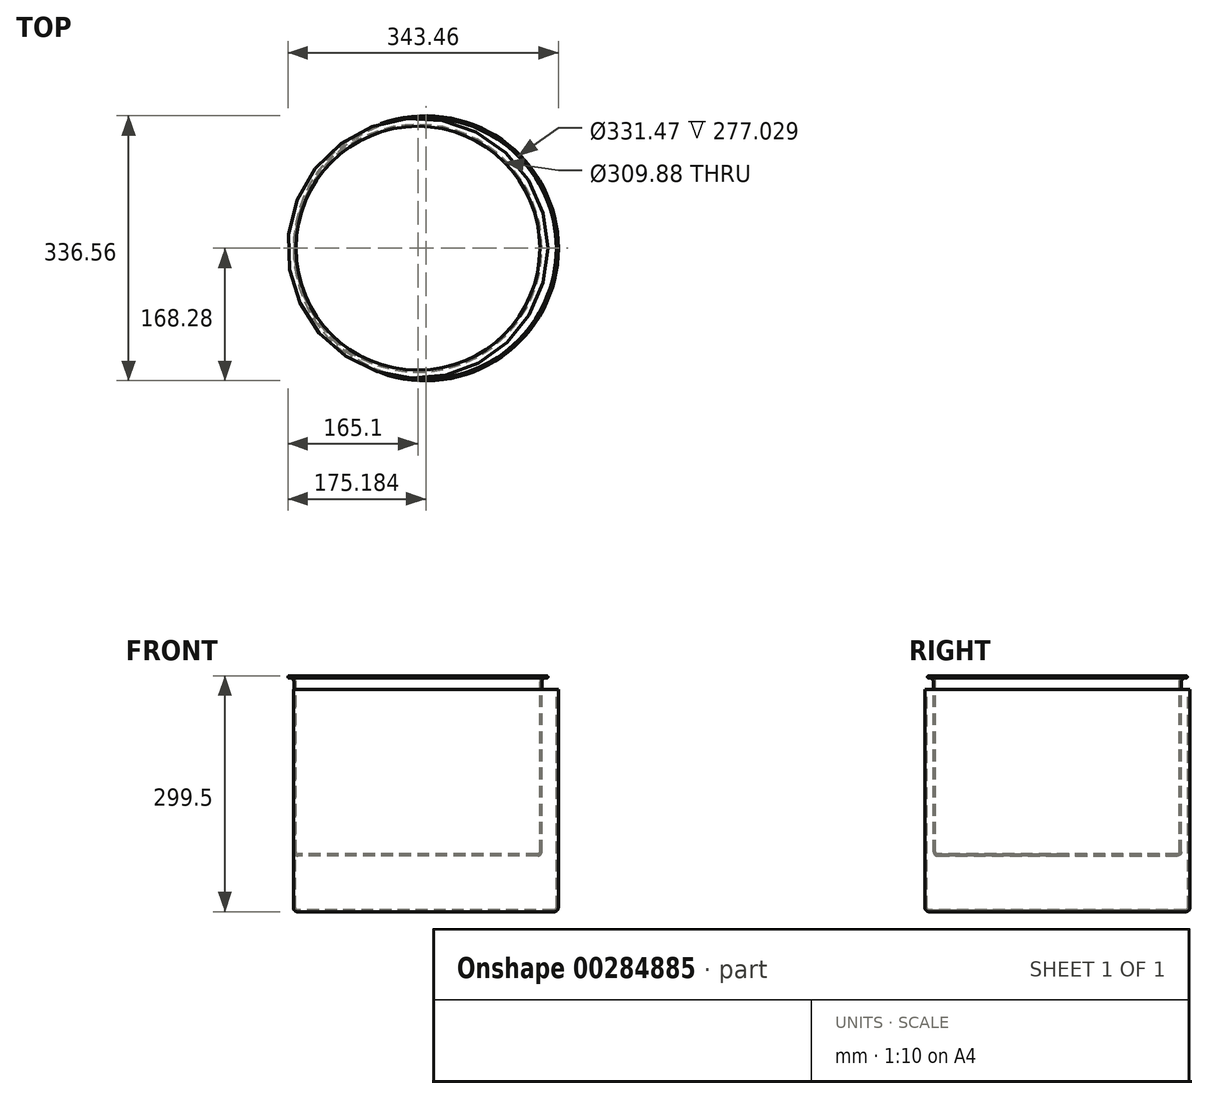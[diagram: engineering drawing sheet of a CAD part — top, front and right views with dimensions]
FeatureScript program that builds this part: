
annotation { "Feature Type Name" : "Feature", "Feature Type Description" : "" }
export const myFeature = defineFeature(function(context is Context, id is Id, definition is map)
    precondition{}
    {
        {
            var Q0;
            Q0=qCreatedBy(makeId("Top.planeOp"),FACE);
            var sketch = newSketch(context, id + "F0", { "sketchPlane" : qUnion([Q0])});
            skCircle(sketch, "E0", {"center": v(0, 0) * mm, "radius": 165.1 * mm});
            skSolve(sketch);
        }
        {
            var Q0;
            Q0 = qSketchRegion(id + "F0", true);
            extrude(context, id + "F1", {"entities" : qUnion([Q0]), "depth" : 2.54 * mm});
        }
        {
            var Q0;
            Q0=makeQuery(id+"F1.opExtrude","CAP_FACE",FACE,{"disambiguationData":[OSD([sQuery(id+"F0.wireOp",EDGE,"E0")])],"isStart":false});
            var sketch = newSketch(context, id + "F2", { "sketchPlane" : qUnion([Q0])});
            skCircle(sketch, "E1", {"center": v(0, 0) * mm, "radius": 165.1 * mm});
            skCircle(sketch, "E2.0", {"center": v(0, 0) * mm, "radius": 162.56 * mm});
            skSolve(sketch);
        }
        {
            var Q0;
            Q0 = qSketchRegion(id + "F2", true);
            extrude(context, id + "F3", {"entities" : qUnion([Q0]), "operationType" : NewBodyOperationType.ADD, "depth" : 228.6 * mm});
        }
        {
            var Q0;
            Q0=qCreatedBy(makeId("Front.planeOp"),FACE);
            var sketch = newSketch(context, id + "F4", { "sketchPlane" : qUnion([Q0])});
            skLineSegment(sketch, "E3", {"start": v(0, 0) * mm, "end": v(-152.4, 0) * mm});
            skLineSegment(sketch, "E4", {"start": v(-157.48, 5.08) * mm, "end": v(-157.48, 220.98) * mm});
            skLineSegment(sketch, "E5", {"start": v(-162.56, 226.06) * mm, "end": v(-163.83, 226.06) * mm});
            skPoint(sketch, "E6.visualSharp", {"position": v(-157.48, 226.06) * mm});
            skArc(sketch, "E6.filletArc", {"start": v(-157.48, 220.98) * mm, "mid": v(-158.97, 224.57) * mm, "end": v(-162.56, 226.06) * mm});
            skPoint(sketch, "E7.visualSharp", {"position": v(-157.48, 0) * mm});
            skArc(sketch, "E7.filletArc", {"start": v(-157.48, 5.08) * mm, "mid": v(-156, 1.49) * mm, "end": v(-152.4, 0) * mm});
            skLineSegment(sketch, "E8.0", {"start": v(-162.56, 228.6) * mm, "end": v(-163.83, 228.6) * mm});
            skArc(sketch, "E8.1", {"start": v(-154.94, 220.98) * mm, "mid": v(-157.17, 226.37) * mm, "end": v(-162.56, 228.6) * mm});
            skLineSegment(sketch, "E8.2", {"start": v(-154.94, 5.08) * mm, "end": v(-154.94, 220.98) * mm});
            skLineSegment(sketch, "E8.3", {"start": v(0, 2.54) * mm, "end": v(-152.4, 2.54) * mm});
            skPoint(sketch, "E9.visualSharp", {"position": v(-154.94, 2.54) * mm});
            skArc(sketch, "E9.filletArc", {"start": v(-154.94, 5.08) * mm, "mid": v(-154.2, 3.28) * mm, "end": v(-152.4, 2.54) * mm});
            skLineSegment(sketch, "E10", {"start": v(0, 2.54) * mm, "end": v(0, 0) * mm});
            skLineSegment(sketch, "E11", {"start": v(-165.1, 227.33) * mm, "end": v(-165.1, 227.33) * mm});
            skPoint(sketch, "E12.visualSharp", {"position": v(-165.1, 228.6) * mm});
            skArc(sketch, "E12.filletArc", {"start": v(-163.83, 228.6) * mm, "mid": v(-164.73, 228.23) * mm, "end": v(-165.1, 227.33) * mm});
            skPoint(sketch, "E13.visualSharp", {"position": v(-165.1, 226.06) * mm});
            skArc(sketch, "E13.filletArc", {"start": v(-165.1, 227.33) * mm, "mid": v(-164.73, 226.43) * mm, "end": v(-163.83, 226.06) * mm});
            skSolve(sketch);
        }
        {
            var Q0;
            Q0=makeQuery(id+"F4.imprint","IMPRINT",FACE,{"disambiguationData":[TD([[makeQuery(id+"F4.imprint","IMPRINT",EDGE,{"derivedFrom":sQuery(id+"F4.wireOp",EDGE,"E3")}),-1.0]])]});
            var Q1;
            Q1=sQuery(id+"F4.wireOp",EDGE,"E10");
            revolve(context, id + "F5", {"entities" : qUnion([Q0]), "axis" : qUnion([Q1]), "revolveType" : RevolveType.FULL});
        }
        {
            var Q0;
            Q0=makeQuery(id+"F1.opExtrude","SWEPT_BODY",BODY,{"disambiguationData":[OSD([sQuery(id+"F0.wireOp",EDGE,"E0")])]});
            deleteBodies(context, id + "F6", {"entities" : qUnion([Q0])});
        }
        {
            var Q0;
            Q0=qCreatedBy(makeId("Front.planeOp"),FACE);
            var sketch = newSketch(context, id + "F7", { "sketchPlane" : qUnion([Q0])});
            skLineSegment(sketch, "E14", {"start": v(10.08, -70.9) * mm, "end": v(-153.11, -70.9) * mm});
            skLineSegment(sketch, "E15", {"start": v(-158.2, -65.82) * mm, "end": v(-158.2, 219.93) * mm});
            skLineSegment(sketch, "E16", {"start": v(-163.27, 225.01) * mm, "end": v(-163.27, 225.01) * mm});
            skPoint(sketch, "E17.visualSharp", {"position": v(-158.2, 225.01) * mm});
            skArc(sketch, "E17.filletArc", {"start": v(-158.2, 219.93) * mm, "mid": v(-159.68, 223.52) * mm, "end": v(-163.27, 225.01) * mm});
            skPoint(sketch, "E18.visualSharp", {"position": v(-158.2, -70.9) * mm});
            skArc(sketch, "E18.filletArc", {"start": v(-158.2, -65.82) * mm, "mid": v(-156.7, -69.41) * mm, "end": v(-153.11, -70.9) * mm});
            skLineSegment(sketch, "E19.0", {"start": v(-163.27, 227.55) * mm, "end": v(-163.27, 227.55) * mm});
            skArc(sketch, "E19.1", {"start": v(-155.65, 219.93) * mm, "mid": v(-157.88, 225.32) * mm, "end": v(-163.27, 227.55) * mm});
            skLineSegment(sketch, "E19.2", {"start": v(-155.65, -65.82) * mm, "end": v(-155.65, 219.93) * mm});
            skLineSegment(sketch, "E19.3", {"start": v(10.08, -68.36) * mm, "end": v(-153.11, -68.36) * mm});
            skPoint(sketch, "E20.visualSharp", {"position": v(-155.65, -68.36) * mm});
            skArc(sketch, "E20.filletArc", {"start": v(-155.65, -65.82) * mm, "mid": v(-154.9, -67.61) * mm, "end": v(-153.11, -68.36) * mm});
            skLineSegment(sketch, "E21", {"start": v(10.08, -68.36) * mm, "end": v(10.08, -70.9) * mm});
            skLineSegment(sketch, "E22", {"start": v(-164.54, 226.28) * mm, "end": v(-164.54, 226.28) * mm});
            skPoint(sketch, "E23.visualSharp", {"position": v(-164.54, 227.55) * mm});
            skArc(sketch, "E23.filletArc", {"start": v(-163.27, 227.55) * mm, "mid": v(-164.17, 227.18) * mm, "end": v(-164.54, 226.28) * mm});
            skPoint(sketch, "E24.visualSharp", {"position": v(-164.54, 225.01) * mm});
            skArc(sketch, "E24.filletArc", {"start": v(-164.54, 226.28) * mm, "mid": v(-164.17, 225.38) * mm, "end": v(-163.27, 225.01) * mm});
            skLineSegment(sketch, "E25", {"start": v(-158.2, 211.21) * mm, "end": v(-155.65, 211.21) * mm});
            skSolve(sketch);
        }
        {
            var Q0;
            Q0=makeQuery(id+"F7.imprint","IMPRINT",FACE,{"disambiguationData":[TD([[makeQuery(id+"F7.imprint","IMPRINT",EDGE,{"derivedFrom":sQuery(id+"F7.wireOp",EDGE,"E14")}),-1.0]])]});
            var Q1;
            Q1=sQuery(id+"F7.wireOp",EDGE,"E21");
            revolve(context, id + "F8", {"surfaceOperationType" : NewSurfaceOperationType.NEW, "entities" : qUnion([Q0]), "axis" : qUnion([Q1]), "revolveType" : RevolveType.FULL});
        }
    });
